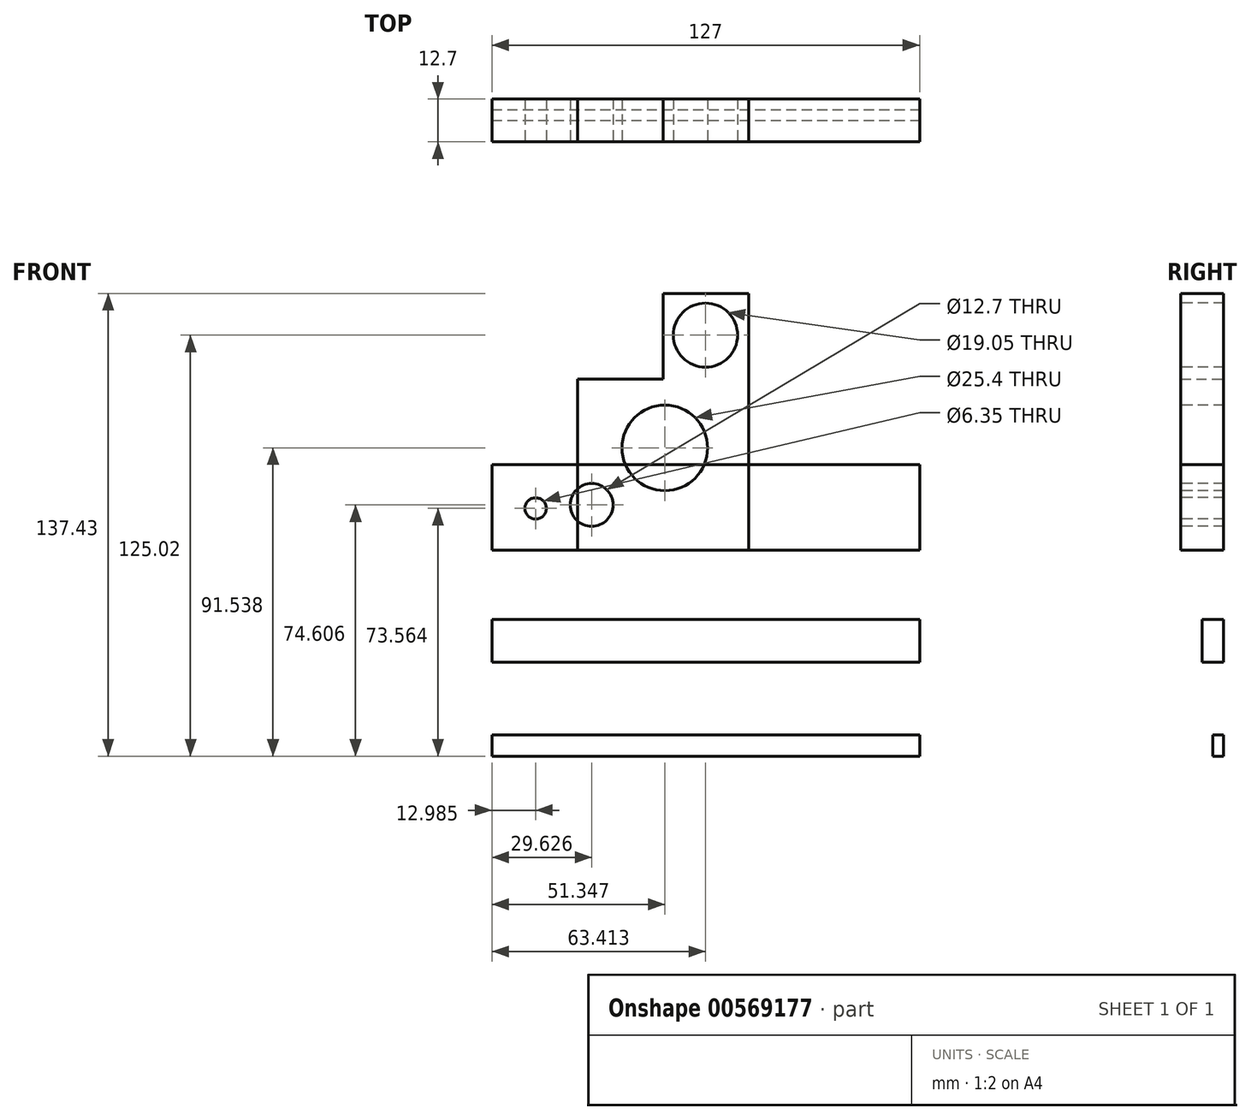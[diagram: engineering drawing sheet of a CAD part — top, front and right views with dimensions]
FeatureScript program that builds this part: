
annotation { "Feature Type Name" : "Feature", "Feature Type Description" : "" }
export const myFeature = defineFeature(function(context is Context, id is Id, definition is map)
    precondition{}
    {
        {
            var Q0;
            Q0=qCreatedBy(makeId("Front.planeOp"),FACE);
            var sketch = newSketch(context, id + "F0", { "sketchPlane" : qUnion([Q0])});
            skLineSegment(sketch, "E0.bottom", {"start": v(0, 0) * mm, "end": v(25.4, 0) * mm});
            skLineSegment(sketch, "E0.top", {"start": v(0, 25.4) * mm, "end": v(25.4, 25.4) * mm});
            skLineSegment(sketch, "E0.left", {"start": v(0, 0) * mm, "end": v(0, 25.4) * mm});
            skLineSegment(sketch, "E0.right", {"start": v(25.4, 0) * mm, "end": v(25.4, 25.4) * mm});
            skLineSegment(sketch, "E1.bottom", {"start": v(25.4, 0) * mm, "end": v(50.8, 0) * mm});
            skLineSegment(sketch, "E1.top", {"start": v(25.4, 50.8) * mm, "end": v(50.8, 50.8) * mm});
            skLineSegment(sketch, "E1.left", {"start": v(25.4, 0) * mm, "end": v(25.4, 50.8) * mm});
            skLineSegment(sketch, "E1.right", {"start": v(50.8, 0) * mm, "end": v(50.8, 50.8) * mm});
            skLineSegment(sketch, "E2.bottom", {"start": v(50.8, 0) * mm, "end": v(76.2, 0) * mm});
            skLineSegment(sketch, "E2.top", {"start": v(50.8, 76.2) * mm, "end": v(76.2, 76.2) * mm});
            skLineSegment(sketch, "E2.left", {"start": v(50.8, 0) * mm, "end": v(50.8, 76.2) * mm});
            skLineSegment(sketch, "E2.right", {"start": v(76.2, 0) * mm, "end": v(76.2, 76.2) * mm});
            skSolve(sketch);
        }
        {
            var Q0;
            Q0 = qSketchRegion(id + "F0", true);
            extrude(context, id + "F1", {"entities" : qUnion([Q0]), "depth" : 12.7 * mm, "offsetDistance" : 25.4 * mm});
        }
        {
            var Q0;
            Q0=makeQuery(id+"F1.opExtrude","CAP_FACE",FACE,{"disambiguationData":[OSD([sQuery(id+"F0.wireOp",EDGE,"E0.bottom"),sQuery(id+"F0.wireOp",EDGE,"E0.top"),sQuery(id+"F0.wireOp",EDGE,"E0.left"),sQuery(id+"F0.wireOp",EDGE,"E1.bottom"),sQuery(id+"F0.wireOp",EDGE,"E1.top"),sQuery(id+"F0.wireOp",EDGE,"E1.left"),sQuery(id+"F0.wireOp",EDGE,"E2.bottom"),sQuery(id+"F0.wireOp",EDGE,"E2.top"),sQuery(id+"F0.wireOp",EDGE,"E2.left"),sQuery(id+"F0.wireOp",EDGE,"E2.right")])],"isStart":false});
            var sketch = newSketch(context, id + "F2", { "sketchPlane" : qUnion([Q0])});
            skCircle(sketch, "E3", {"center": v(12.99, 12.33) * mm, "radius": 3.18 * mm});
            skCircle(sketch, "E4", {"center": v(29.63, 13.38) * mm, "radius": 6.35 * mm});
            skCircle(sketch, "E5", {"center": v(63.41, 63.79) * mm, "radius": 9.53 * mm});
            skCircle(sketch, "E6", {"center": v(51.35, 30.3) * mm, "radius": 12.7 * mm});
            skSolve(sketch);
        }
        {
            var Q0;
            Q0 = qSketchRegion(id + "F2", true);
            extrude(context, id + "F3", {"entities" : qUnion([Q0]), "operationType" : NewBodyOperationType.REMOVE, "oppositeDirection" : true, "depth" : 170.7 * mm, "offsetDistance" : 25.4 * mm});
        }
        {
            var Q0;
            Q0=qCreatedBy(makeId("Front.planeOp"),FACE);
            var sketch = newSketch(context, id + "F4", { "sketchPlane" : qUnion([Q0])});
            skLineSegment(sketch, "E7.bottom", {"start": v(0, 0) * mm, "end": v(127, 0) * mm});
            skLineSegment(sketch, "E7.top", {"start": v(0, 25.4) * mm, "end": v(127, 25.4) * mm});
            skLineSegment(sketch, "E7.left", {"start": v(0, 0) * mm, "end": v(0, 25.4) * mm});
            skLineSegment(sketch, "E7.right", {"start": v(127, 0) * mm, "end": v(127, 25.4) * mm});
            skLineSegment(sketch, "E8.bottom", {"start": v(0, -20.6) * mm, "end": v(127, -20.6) * mm});
            skLineSegment(sketch, "E8.top", {"start": v(0, -33.3) * mm, "end": v(127, -33.3) * mm});
            skLineSegment(sketch, "E8.left", {"start": v(0, -20.6) * mm, "end": v(0, -33.3) * mm});
            skLineSegment(sketch, "E8.right", {"start": v(127, -20.6) * mm, "end": v(127, -33.3) * mm});
            skLineSegment(sketch, "E9.bottom", {"start": v(0, -54.88) * mm, "end": v(127, -54.88) * mm});
            skLineSegment(sketch, "E9.top", {"start": v(0, -61.23) * mm, "end": v(127, -61.23) * mm});
            skLineSegment(sketch, "E9.left", {"start": v(0, -54.88) * mm, "end": v(0, -61.23) * mm});
            skLineSegment(sketch, "E9.right", {"start": v(127, -54.88) * mm, "end": v(127, -61.23) * mm});
            skSolve(sketch);
        }
        {
            var Q0;
            Q0=makeQuery(id+"F4.imprint","IMPRINT",FACE,{"disambiguationData":[TD([[makeQuery(id+"F4.imprint","IMPRINT",EDGE,{"derivedFrom":sQuery(id+"F4.wireOp",EDGE,"E7.bottom")}),1.0]])]});
            extrude(context, id + "F5", {"entities" : qUnion([Q0]), "depth" : 12.7 * mm, "offsetDistance" : 25.4 * mm});
        }
        {
            var Q0;
            Q0=makeQuery(id+"F4.imprint","IMPRINT",FACE,{"disambiguationData":[TD([[makeQuery(id+"F4.imprint","IMPRINT",EDGE,{"derivedFrom":sQuery(id+"F4.wireOp",EDGE,"E8.bottom")}),-1.0]])]});
            extrude(context, id + "F6", {"entities" : qUnion([Q0]), "depth" : 6.35 * mm, "offsetDistance" : 25.4 * mm});
        }
        {
            var Q0;
            Q0=makeQuery(id+"F4.imprint","IMPRINT",FACE,{"disambiguationData":[TD([[makeQuery(id+"F4.imprint","IMPRINT",EDGE,{"derivedFrom":sQuery(id+"F4.wireOp",EDGE,"E9.bottom")}),-1.0]])]});
            extrude(context, id + "F7", {"entities" : qUnion([Q0]), "depth" : 3.17 * mm, "offsetDistance" : 25.4 * mm});
        }
        {
            var Q0;
            Q0=qCreatedBy(makeId("Front.planeOp"), FACE);
            var sketch = newSketch(context, id + "F8", { "sketchPlane" : qUnion([Q0])});
            skLineSegment(sketch, "E10.bottom", {"start": v(0, 0) * mm, "end": v(25.4, 0) * mm});
            skLineSegment(sketch, "E10.top", {"start": v(0, 25.4) * mm, "end": v(25.4, 25.4) * mm});
            skLineSegment(sketch, "E10.left", {"start": v(0, 0) * mm, "end": v(0, 25.4) * mm});
            skLineSegment(sketch, "E10.right", {"start": v(25.4, 0) * mm, "end": v(25.4, 25.4) * mm});
            skSolve(sketch);
        }
        {
            var Q0;
            Q0 = qSketchRegion(id + "F8", true);
            extrude(context, id + "F9", {"entities" : qUnion([Q0]), "domain" : OperationDomain.MODEL, "flatOperationType" : FlatOperationType.REMOVE, "depth" : 12.7 * mm, "offsetDistance" : 25.4 * mm});
        }
    });
